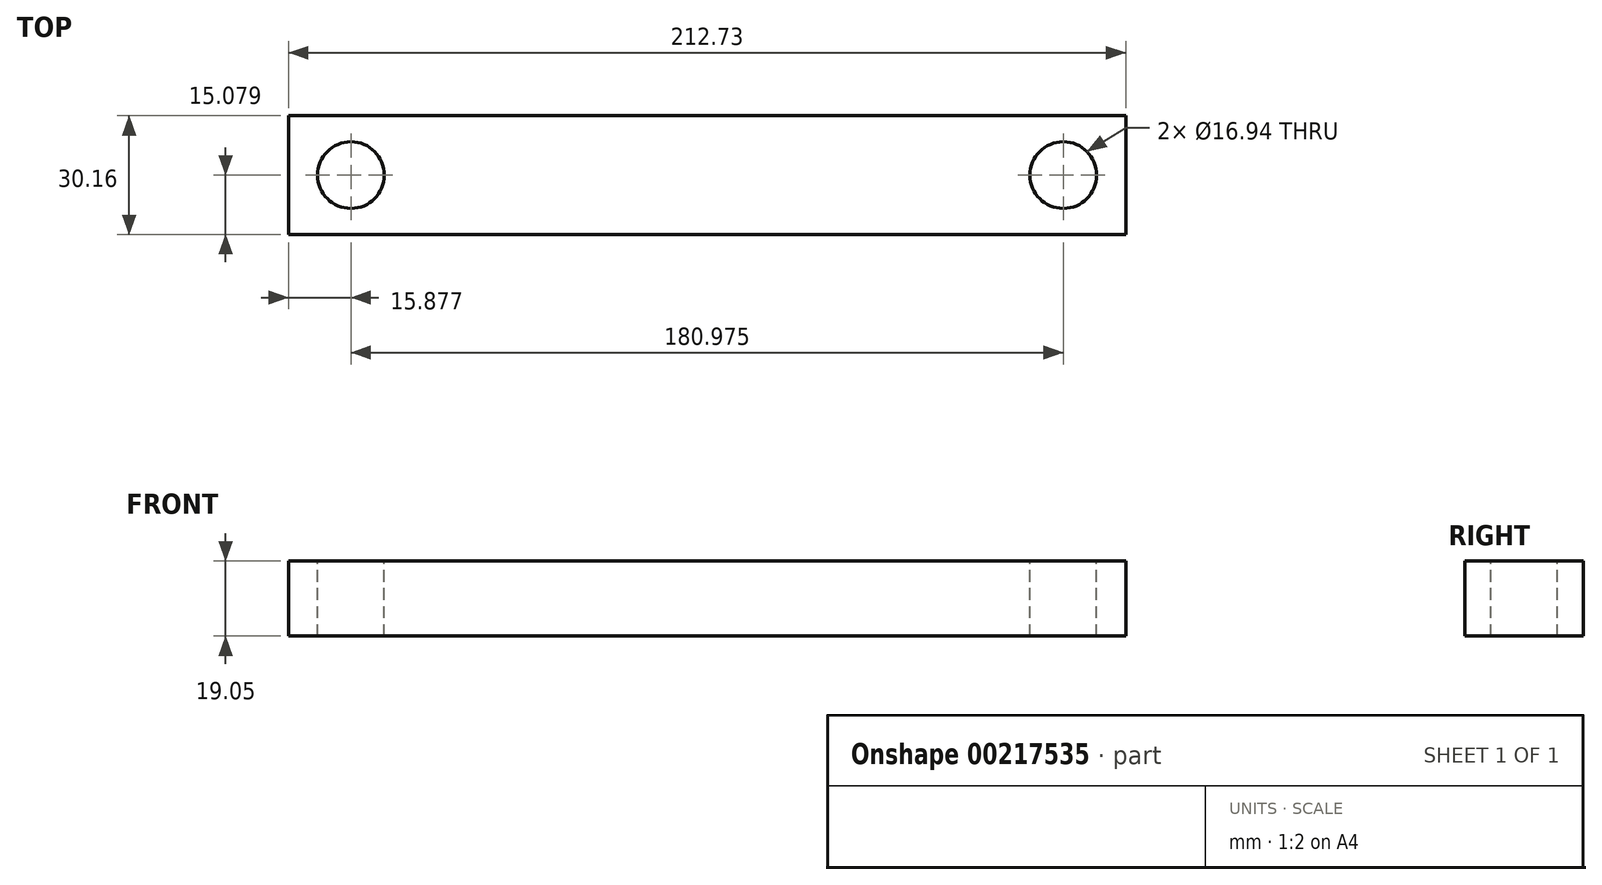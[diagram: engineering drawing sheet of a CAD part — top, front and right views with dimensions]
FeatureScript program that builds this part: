
annotation { "Feature Type Name" : "Feature", "Feature Type Description" : "" }
export const myFeature = defineFeature(function(context is Context, id is Id, definition is map)
    precondition{}
    {
        {
            var Q0;
            Q0=qCreatedBy(makeId("Front.planeOp"),FACE);
            var sketch = newSketch(context, id + "F0", { "sketchPlane" : qUnion([Q0])});
            skLineSegment(sketch, "E0.bottom", {"start": v(-20.28, 11.46) * mm, "end": v(192.45, 11.46) * mm});
            skLineSegment(sketch, "E0.top", {"start": v(-20.28, -7.59) * mm, "end": v(192.45, -7.59) * mm});
            skLineSegment(sketch, "E0.left", {"start": v(-20.28, 11.46) * mm, "end": v(-20.28, -7.59) * mm});
            skLineSegment(sketch, "E0.right", {"start": v(192.45, 11.46) * mm, "end": v(192.45, -7.59) * mm});
            skSolve(sketch);
        }
        {
            var Q0;
            Q0 = qSketchRegion(id + "F0", true);
            extrude(context, id + "F1", {"entities" : qUnion([Q0]), "depth" : 30.16 * mm});
        }
        {
            var Q0;
            Q0=makeQuery(id+"F1.opExtrude","SWEPT_FACE",FACE,{"disambiguationData":[OSD([sQuery(id+"F0.wireOp",EDGE,"E0.bottom")])]});
            var sketch = newSketch(context, id + "F2", { "sketchPlane" : qUnion([Q0])});
            skCircle(sketch, "E1", {"center": v(-4.4, -15.08) * mm, "radius": 8.47 * mm});
            skPoint(sketch, "E1.centerSnap0", {"position": v(-20.28, -15.08) * mm});
            skCircle(sketch, "E2", {"center": v(176.57, -15.08) * mm, "radius": 8.47 * mm});
            skSolve(sketch);
        }
        {
            var Q0;
            Q0 = qSketchRegion(id + "F2", true);
            extrude(context, id + "F3", {"entities" : qUnion([Q0]), "operationType" : NewBodyOperationType.REMOVE, "oppositeDirection" : true, "depth" : 25.4 * mm});
        }
    });
